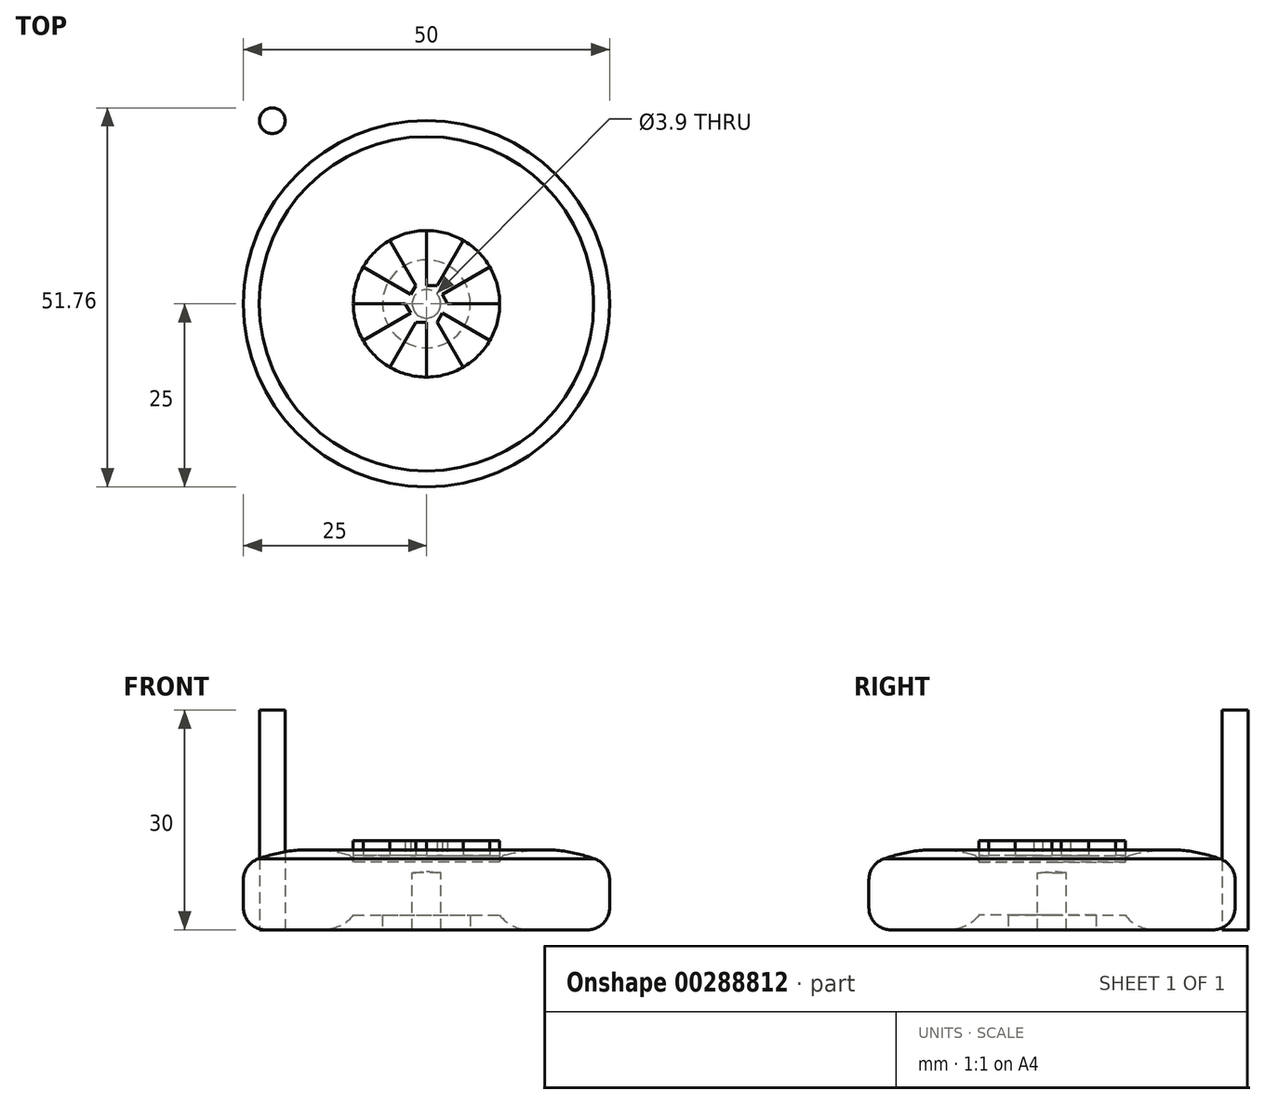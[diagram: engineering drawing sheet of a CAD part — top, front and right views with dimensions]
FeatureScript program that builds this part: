
annotation { "Feature Type Name" : "Feature", "Feature Type Description" : "" }
export const myFeature = defineFeature(function(context is Context, id is Id, definition is map)
    precondition{}
    {
        {
            var Q0;
            Q0=qCreatedBy(makeId("Top.planeOp"),FACE);
            var sketch = newSketch(context, id + "F0", { "sketchPlane" : qUnion([Q0])});
            skCircle(sketch, "E0", {"center": v(-21.06, 25) * mm, "radius": 1.75 * mm});
            skSolve(sketch);
        }
        {
            var Q0;
            Q0=makeQuery(id+"F0.imprint","IMPRINT",FACE,{"disambiguationData":[TD([[makeQuery(id+"F0.imprint","IMPRINT",EDGE,{"derivedFrom":sQuery(id+"F0.wireOp",EDGE,"E0")}),1.0]])]});
            extrude(context, id + "F1", {"entities" : qUnion([Q0]), "depth" : 30 * mm});
        }
        {
            var Q0;
            Q0=qCreatedBy(makeId("Front.planeOp"),FACE);
            var sketch = newSketch(context, id + "F2", { "sketchPlane" : qUnion([Q0])});
            skLineSegment(sketch, "E1", {"start": v(0, 0) * mm, "end": v(0, 8) * mm});
            skLineSegment(sketch, "E2", {"start": v(25, 6.83) * mm, "end": v(25, 3) * mm});
            skLineSegment(sketch, "E3", {"start": v(22, 0) * mm, "end": v(10, 0) * mm});
            skLineSegment(sketch, "E4", {"start": v(10, 0) * mm, "end": v(10, 2) * mm});
            skLineSegment(sketch, "E5", {"start": v(10, 2) * mm, "end": v(6, 2) * mm});
            skLineSegment(sketch, "E6", {"start": v(6, 2) * mm, "end": v(6, 0) * mm});
            skPoint(sketch, "E7.visualSharp", {"position": v(25, 0) * mm});
            skArc(sketch, "E7.filletArc", {"start": v(22, 0) * mm, "mid": v(24.12, 0.88) * mm, "end": v(25, 3) * mm});
            skPoint(sketch, "E8.visualSharp", {"position": v(25, 10) * mm});
            skArc(sketch, "E8.filletArc", {"start": v(25, 6.83) * mm, "mid": v(24.4, 8.64) * mm, "end": v(22.83, 9.72) * mm});
            skArc(sketch, "E9", {"start": v(22.83, 9.72) * mm, "mid": v(16.44, 10.92) * mm, "end": v(10, 10) * mm});
            skPoint(sketch, "E10.visualSharp", {"position": v(10, 0) * mm});
            skFitSpline(sketch, "E11", {"points": [v(0, 8) * mm, v(6, 8) * mm, v(7.6, 9) * mm, v(10, 10) * mm], "startDerivative": vector(24.02, -3.4) * mm, "endDerivative": vector(6.99, 1.38) * mm});
            skLineSegment(sketch, "E12", {"start": v(0, 0) * mm, "end": v(6, 0) * mm});
            skLineSegment(sketch, "E13", {"start": v(10, 10) * mm, "end": v(10, 5.14) * mm});
            skLineSegment(sketch, "E14", {"start": v(10, 5.14) * mm, "end": v(4, 5.14) * mm});
            skLineSegment(sketch, "E15", {"start": v(4, 5.14) * mm, "end": v(4, 7.64) * mm});
            skSolve(sketch);
        }
        {
            var Q0;
            Q0=makeQuery(id+"F2.imprint","IMPRINT",FACE,{"disambiguationData":[TD([[makeQuery(id+"F2.imprint","IMPRINT",EDGE,{"derivedFrom":sQuery(id+"F2.wireOp",EDGE,"E1")}),-1.0]])]});
            var Q1;
            Q1=sQuery(id+"F2.wireOp",EDGE,"E1");
            revolve(context, id + "F3", {"entities" : qUnion([Q0]), "axis" : qUnion([Q1]), "revolveType" : RevolveType.FULL});
        }
        {
            var Q0;
            Q0=makeQuery(id+"F3.opRevolve","SWEPT_EDGE",EDGE,{"disambiguationData":[OSD([sQuery(id+"F2.wireOp",EDGE,"E3"),sQuery(id+"F2.wireOp",EDGE,"E4")])]});
            fillet(context, id + "F4", {"entities" : qUnion([Q0]), "radius" : 5 * mm, "tangentPropagation" : true, "allowEdgeOverflow" : false});
        }
        {
            var Q0;
            Q0=qCreatedBy(makeId("Top.planeOp"),FACE);
            var sketch = newSketch(context, id + "F5", { "sketchPlane" : qUnion([Q0])});
            skPoint(sketch, "E16", {"position": v(0, 0) * mm});
            skSolve(sketch);
        }
        {
            var Q0;
            Q0=sQuery(id+"F5.wireOp",VERTEX,"E16");
            var Q1;
            Q1=makeQuery(id+"F3.opRevolve","SWEPT_BODY",BODY,{"disambiguationData":[OSD([sQuery(id+"F2.wireOp",EDGE,"E1"),sQuery(id+"F2.wireOp",EDGE,"E2"),sQuery(id+"F2.wireOp",EDGE,"E3"),sQuery(id+"F2.wireOp",EDGE,"E4"),sQuery(id+"F2.wireOp",EDGE,"E5"),sQuery(id+"F2.wireOp",EDGE,"E6"),sQuery(id+"F2.wireOp",EDGE,"Q9cDsmCs-q79E-soxS-GJNm-XGcUUAOyhzII"),sQuery(id+"F2.wireOp",EDGE,"E7.filletArc"),sQuery(id+"F2.wireOp",EDGE,"E8.filletArc"),sQuery(id+"F2.wireOp",EDGE,"E9"),sQuery(id+"F2.wireOp",EDGE,"E11")])]});
            hole(context, id + "F6", {"style" : HoleStyle.SIMPLE, "endStyle" : HoleEndStyle.THROUGH, "oppositeDirection" : true, "holeDiameter" : 3.9 * mm, "startFromSketch" : true, "locations" : qUnion([Q0]), "scope" : qUnion([Q1]), "tappedDepth" : 12 * mm, "tapClearance" : 3});
        }
        {
            var Q0;
            Q0=makeQuery(id+"F3.opRevolve","SWEPT_FACE",FACE,{"disambiguationData":[OSD([sQuery(id+"F2.wireOp",EDGE,"E14")])]});
            extrude(context, id + "F7", {"entities" : qUnion([Q0]), "depth" : 5 * mm});
        }
        {
            var Q0;
            Q0=makeQuery(id+"F3.opRevolve","SWEPT_EDGE",EDGE,{"disambiguationData":[OSD([sQuery(id+"F2.wireOp",EDGE,"E9"),sQuery(id+"F2.wireOp",EDGE,"E11"),sQuery(id+"F2.wireOp",EDGE,"E13")])]});
            fillet(context, id + "F8", {"entities" : qUnion([Q0]), "radius" : 1 * mm, "tangentPropagation" : true, "allowEdgeOverflow" : false});
        }
        {
            var Q0;
            Q0=makeQuery(id+"F7.opExtrude","CAP_FACE",FACE,{"disambiguationData":[OSD([sQuery(id+"F2.wireOp",EDGE,"E14")])],"isStart":false});
            var sketch = newSketch(context, id + "F9", { "sketchPlane" : qUnion([Q0])});
            skCircle(sketch, "E17", {"center": v(0, 0) * mm, "radius": 4 * mm});
            skCircle(sketch, "E18", {"center": v(0, 0) * mm, "radius": 10 * mm});
            skCircle(sketch, "E19", {"center": v(0, 0) * mm, "radius": 1.95 * mm});
            skSolve(sketch);
        }
        {
            var Q0;
            Q0=makeQuery(id+"F9.imprint","IMPRINT",FACE,{"disambiguationData":[TD([[makeQuery(id+"F9.imprint","IMPRINT",EDGE,{"derivedFrom":sQuery(id+"F9.wireOp",EDGE,"E17")}),-1.0]])]});
            var Q1;
            Q1=makeQuery(id+"F9.imprint","IMPRINT",FACE,{"disambiguationData":[TD([[makeQuery(id+"F9.imprint","IMPRINT",EDGE,{"derivedFrom":sQuery(id+"F9.wireOp",EDGE,"E19")}),1.0]])]});
            var Q2;
            Q2=makeQuery(id+"F3.opRevolve","SWEPT_FACE",FACE,{"disambiguationData":[OSD([sQuery(id+"F2.wireOp",EDGE,"E11")])]});
            extrude(context, id + "F10", {"entities" : qUnion([Q0, Q1]), "operationType" : NewBodyOperationType.ADD, "endBound" : BoundingType.UP_TO_SURFACE, "oppositeDirection" : true, "endBoundEntityFace" : qUnion([Q2]), "depth" : 25 * mm});
        }
        {
            var Q0;
            Q0=makeQuery(id+"F10.boolean.opBoolean","MERGE",FACE,{"derivedFrom":[makeQuery(id+"F7.opExtrude","CAP_FACE",FACE,{"disambiguationData":[OSD([sQuery(id+"F2.wireOp",EDGE,"E14")])],"isStart":false}),makeQuery(id+"F10.opExtrude","CAP_FACE",FACE,{"disambiguationData":[OSD([sQuery(id+"F9.wireOp",EDGE,"E17")])],"isStart":true})]});
            var sketch = newSketch(context, id + "F11", { "sketchPlane" : qUnion([Q0])});
            skCircle(sketch, "E20.cCircle", {"center": v(0, 0) * mm, "radius": 2.5 * mm, "construction": true});
            skLineSegment(sketch, "E20.0", {"start": v(-2.89, 0) * mm, "end": v(-1.44, 2.5) * mm});
            skLineSegment(sketch, "E20.1", {"start": v(-1.44, 2.5) * mm, "end": v(1.44, 2.5) * mm});
            skLineSegment(sketch, "E20.2", {"start": v(1.44, 2.5) * mm, "end": v(2.89, 0) * mm});
            skLineSegment(sketch, "E20.3", {"start": v(2.89, 0) * mm, "end": v(1.44, -2.5) * mm});
            skLineSegment(sketch, "E20.4", {"start": v(1.44, -2.5) * mm, "end": v(-1.44, -2.5) * mm});
            skLineSegment(sketch, "E20.5", {"start": v(-1.44, -2.5) * mm, "end": v(-2.89, 0) * mm});
            skPoint(sketch, "E20.0.midPoint", {"position": v(-2.17, 1.25) * mm});
            skLineSegment(sketch, "E21", {"start": v(1.44, 2.5) * mm, "end": v(5, 8.66) * mm});
            skLineSegment(sketch, "E22", {"start": v(2.89, 0) * mm, "end": v(10, 0) * mm});
            skLineSegment(sketch, "E23", {"start": v(1.44, -2.5) * mm, "end": v(5, -8.66) * mm});
            skLineSegment(sketch, "E24", {"start": v(-1.44, -2.5) * mm, "end": v(-5, -8.66) * mm});
            skLineSegment(sketch, "E25", {"start": v(-2.89, 0) * mm, "end": v(-10, 0) * mm});
            skLineSegment(sketch, "E26", {"start": v(-1.44, 2.5) * mm, "end": v(-5, 8.66) * mm});
            skLineSegment(sketch, "E27", {"start": v(0, 2.5) * mm, "end": v(0, 10) * mm});
            skLineSegment(sketch, "E28", {"start": v(0, -2.5) * mm, "end": v(0, -10) * mm});
            skLineSegment(sketch, "E29", {"start": v(-2.17, -1.25) * mm, "end": v(-8.66, -5) * mm});
            skLineSegment(sketch, "E30", {"start": v(2.17, -1.25) * mm, "end": v(8.66, -5) * mm});
            skLineSegment(sketch, "E31", {"start": v(2.17, 1.25) * mm, "end": v(8.66, 5) * mm});
            skLineSegment(sketch, "E32", {"start": v(-2.17, 1.25) * mm, "end": v(-8.66, 5) * mm});
            skSolve(sketch);
        }
        {
            var Q0;
            {var subQ0=sQuery(id+"F11.wireOp",EDGE,"E26");Q0=makeQuery(id+"F11.imprint","IMPRINT",FACE,{"disambiguationData":[TD([[makeQuery(id+"F11.imprint","IMPRINT",EDGE,{"derivedFrom":subQ0}),-1.0]])]});}
            var Q1;
            {var subQ0=sQuery(id+"F11.wireOp",EDGE,"E21");Q1=makeQuery(id+"F11.imprint","IMPRINT",FACE,{"disambiguationData":[TD([[makeQuery(id+"F11.imprint","IMPRINT",EDGE,{"derivedFrom":subQ0}),-1.0]])]});}
            var Q2;
            {var subQ0=sQuery(id+"F11.wireOp",EDGE,"E22");Q2=makeQuery(id+"F11.imprint","IMPRINT",FACE,{"disambiguationData":[TD([[makeQuery(id+"F11.imprint","IMPRINT",EDGE,{"derivedFrom":subQ0}),-1.0]])]});}
            var Q3;
            {var subQ0=sQuery(id+"F11.wireOp",EDGE,"E23");Q3=makeQuery(id+"F11.imprint","IMPRINT",FACE,{"disambiguationData":[TD([[makeQuery(id+"F11.imprint","IMPRINT",EDGE,{"derivedFrom":subQ0}),-1.0]])]});}
            var Q4;
            {var subQ0=sQuery(id+"F11.wireOp",EDGE,"E24");Q4=makeQuery(id+"F11.imprint","IMPRINT",FACE,{"disambiguationData":[TD([[makeQuery(id+"F11.imprint","IMPRINT",EDGE,{"derivedFrom":subQ0}),-1.0]])]});}
            var Q5;
            {var subQ0=sQuery(id+"F11.wireOp",EDGE,"E25");Q5=makeQuery(id+"F11.imprint","IMPRINT",FACE,{"disambiguationData":[TD([[makeQuery(id+"F11.imprint","IMPRINT",EDGE,{"derivedFrom":subQ0}),-1.0]])]});}
            var Q6;
            {var subQ12=sQuery(id+"F11.wireOp",EDGE,"E20.0");var subQ14=makeQuery(id+"F11.imprint","INTERSECT",VERTEX,{"derivedFrom":[subQ12,sQuery(id+"F11.wireOp",EDGE,"E32")]});Q6=makeQuery(id+"F11.imprint","IMPRINT",FACE,{"disambiguationData":[TD([[makeQuery(id+"F11.imprint","IMPRINT",EDGE,{"disambiguationData":[TD([[subQ14,1.0]])],"derivedFrom":subQ12}),-1.0]])]});}
            extrude(context, id + "F12", {"entities" : qUnion([Q0, Q1, Q2, Q3, Q4, Q5, Q6]), "operationType" : NewBodyOperationType.ADD, "depth" : 2 * mm});
        }
    });
